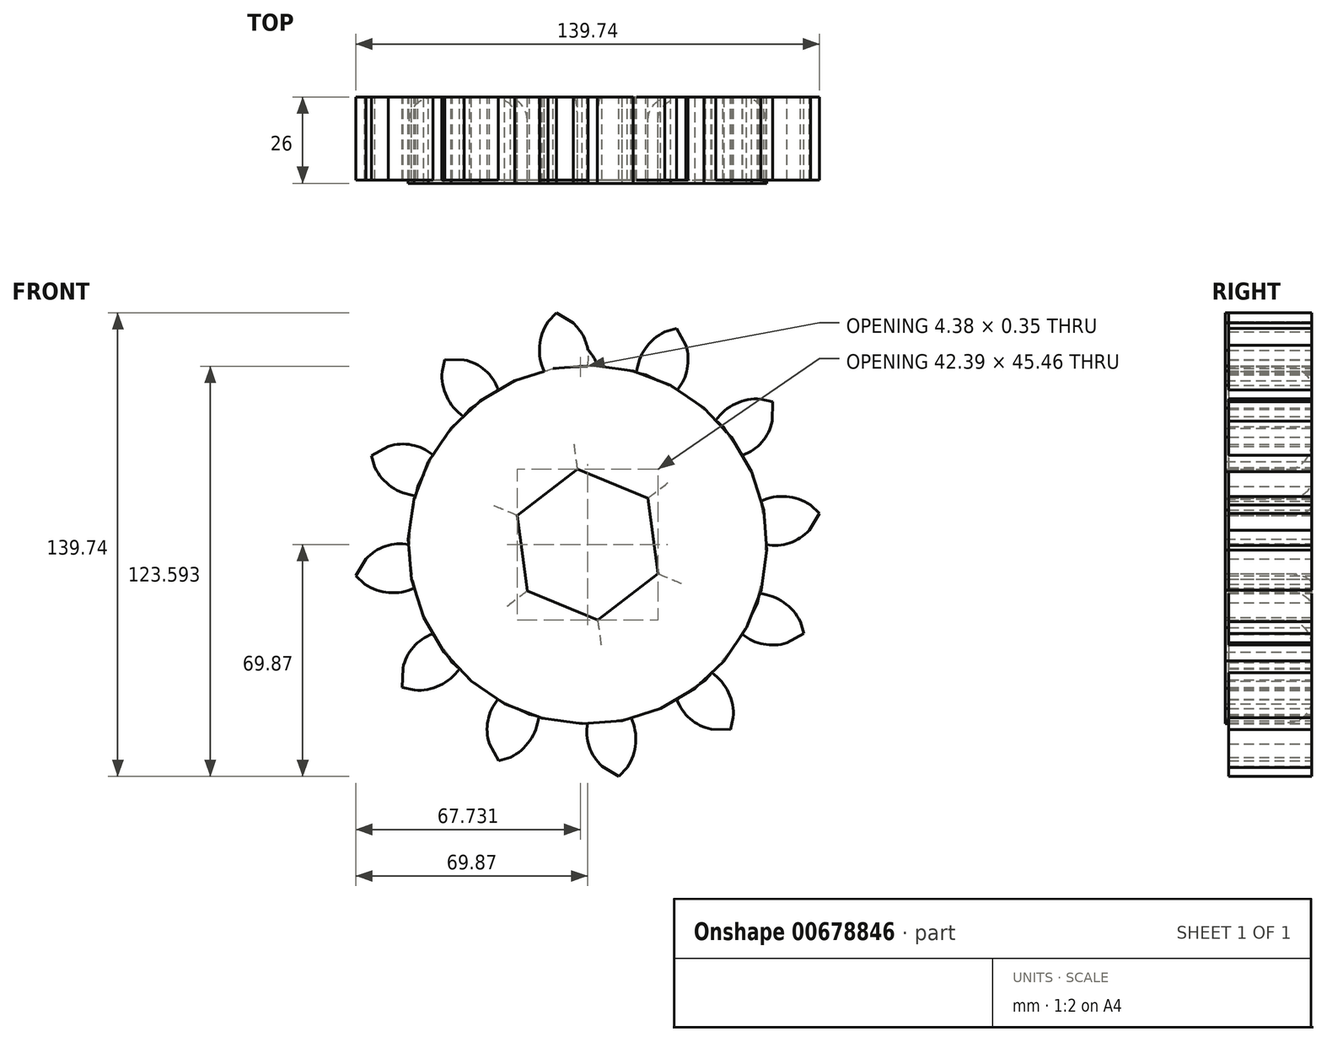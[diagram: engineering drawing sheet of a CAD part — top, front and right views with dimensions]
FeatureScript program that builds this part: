
annotation { "Feature Type Name" : "Feature", "Feature Type Description" : "" }
export const myFeature = defineFeature(function(context is Context, id is Id, definition is map)
    precondition{}
    {
        {
            var Q0;
            Q0=qCreatedBy(makeId("Front.planeOp"),FACE);
            var sketch = newSketch(context, id + "F0", { "sketchPlane" : qUnion([Q0])});
            skCircle(sketch, "E0", {"center": v(0, 0) * mm, "radius": 53.72 * mm, "construction": true});
            skCircle(sketch, "E1", {"center": v(0, 0) * mm, "radius": 58.67 * mm, "construction": true});
            skCircle(sketch, "E2", {"center": v(0, 0) * mm, "radius": 63.5 * mm, "construction": true});
            skLineSegment(sketch, "E3", {"start": v(0, 0) * mm, "end": v(0, 75.67) * mm, "construction": true});
            skLineSegment(sketch, "E4", {"start": v(0, 0) * mm, "end": v(-5.82, 88.8) * mm, "construction": true});
            skLineSegment(sketch, "E5", {"start": v(0, 58.67) * mm, "end": v(-75.23, 45.45) * mm, "construction": true});
            skLineSegment(sketch, "E6", {"start": v(0, 58.67) * mm, "end": v(-71.15, 58.67) * mm, "construction": true});
            skCircle(sketch, "E7", {"center": v(0, 0) * mm, "radius": 57.79 * mm, "construction": true});
            skCircle(sketch, "E8", {"center": v(0, 58.67) * mm, "radius": 14.6 * mm, "construction": true});
            skCircle(sketch, "E9", {"center": v(-14.38, 56.14) * mm, "radius": 14.6 * mm, "construction": true});
            skArc(sketch, "E10", {"start": v(0, 44.07) * mm, "mid": v(3.24, 51.37) * mm, "end": v(0, 58.67) * mm});
            skLineSegment(sketch, "E11.MirrorCS", {"start": v(0, 0) * mm, "end": v(5.82, 88.8) * mm, "construction": true});
            skArc(sketch, "E12", {"start": v(0.02, 53.72) * mm, "mid": v(-0.47, 60.83) * mm, "end": v(-4.38, 66.78) * mm});
            skArc(sketch, "E13", {"start": v(-11.9, 67.15) * mm, "mid": v(-14.49, 59.78) * mm, "end": v(-13.05, 52.11) * mm});
            skLineSegment(sketch, "E14", {"start": v(-11.9, 67.15) * mm, "end": v(-9.38, 69.87) * mm});
            skLineSegment(sketch, "E15", {"start": v(-9.38, 69.87) * mm, "end": v(-4.38, 66.78) * mm});
            skLineSegment(sketch, "E16.0", {"start": v(35.02, 41.18) * mm, "end": v(43.3, 32.36) * mm});
            skLineSegment(sketch, "E16.1", {"start": v(43.3, 32.36) * mm, "end": v(49.42, 21.91) * mm});
            skLineSegment(sketch, "E16.2", {"start": v(49.42, 21.91) * mm, "end": v(53.06, 10.36) * mm});
            skLineSegment(sketch, "E16.3", {"start": v(53.06, 10.36) * mm, "end": v(54.03, -1.7) * mm});
            skLineSegment(sketch, "E16.4", {"start": v(54.03, -1.7) * mm, "end": v(52.3, -13.68) * mm});
            skLineSegment(sketch, "E16.5", {"start": v(52.3, -13.68) * mm, "end": v(47.94, -24.98) * mm});
            skLineSegment(sketch, "E16.6", {"start": v(47.94, -24.98) * mm, "end": v(41.18, -35.02) * mm});
            skLineSegment(sketch, "E16.7", {"start": v(41.18, -35.02) * mm, "end": v(32.36, -43.3) * mm});
            skLineSegment(sketch, "E16.8", {"start": v(32.36, -43.3) * mm, "end": v(21.91, -49.42) * mm});
            skLineSegment(sketch, "E16.9", {"start": v(21.91, -49.42) * mm, "end": v(10.36, -53.06) * mm});
            skLineSegment(sketch, "E16.10", {"start": v(10.36, -53.06) * mm, "end": v(-1.7, -54.03) * mm});
            skLineSegment(sketch, "E16.11", {"start": v(-1.7, -54.03) * mm, "end": v(-13.68, -52.3) * mm});
            skLineSegment(sketch, "E16.12", {"start": v(-13.68, -52.3) * mm, "end": v(-24.98, -47.94) * mm});
            skLineSegment(sketch, "E16.13", {"start": v(-24.98, -47.94) * mm, "end": v(-35.02, -41.18) * mm});
            skLineSegment(sketch, "E16.14", {"start": v(-35.02, -41.18) * mm, "end": v(-43.3, -32.36) * mm});
            skLineSegment(sketch, "E16.15", {"start": v(-43.3, -32.36) * mm, "end": v(-49.42, -21.91) * mm});
            skLineSegment(sketch, "E16.16", {"start": v(-49.42, -21.91) * mm, "end": v(-53.06, -10.36) * mm});
            skLineSegment(sketch, "E16.17", {"start": v(-53.06, -10.36) * mm, "end": v(-54.03, 1.7) * mm});
            skLineSegment(sketch, "E16.18", {"start": v(-54.03, 1.7) * mm, "end": v(-52.3, 13.68) * mm});
            skLineSegment(sketch, "E16.19", {"start": v(-52.3, 13.68) * mm, "end": v(-47.94, 24.98) * mm});
            skLineSegment(sketch, "E16.20", {"start": v(-47.94, 24.98) * mm, "end": v(-41.18, 35.02) * mm});
            skLineSegment(sketch, "E16.21", {"start": v(-41.18, 35.02) * mm, "end": v(-32.36, 43.3) * mm});
            skLineSegment(sketch, "E16.22", {"start": v(-32.36, 43.3) * mm, "end": v(-21.91, 49.42) * mm});
            skLineSegment(sketch, "E16.23", {"start": v(-21.91, 49.42) * mm, "end": v(-10.36, 53.06) * mm});
            skLineSegment(sketch, "E16.24", {"start": v(-10.36, 53.06) * mm, "end": v(1.7, 54.03) * mm});
            skLineSegment(sketch, "E16.25", {"start": v(1.7, 54.03) * mm, "end": v(13.68, 52.3) * mm});
            skLineSegment(sketch, "E16.26", {"start": v(13.68, 52.3) * mm, "end": v(24.98, 47.94) * mm});
            skLineSegment(sketch, "E16.27", {"start": v(24.98, 47.94) * mm, "end": v(35.02, 41.18) * mm});
            skPoint(sketch, "E16.0.midPoint", {"position": v(39.16, 36.77) * mm});
            skCircle(sketch, "E17", {"center": v(0, 0) * mm, "radius": 53.72 * mm});
            skCircle(sketch, "E18", {"center": v(0, 0) * mm, "radius": 38.98 * mm});
            skCircle(sketch, "E19.cCircle", {"center": v(0, 0) * mm, "radius": 19.86 * mm, "construction": true});
            skLineSegment(sketch, "E19.0", {"start": v(-3.02, 22.73) * mm, "end": v(18.17, 13.98) * mm});
            skLineSegment(sketch, "E19.1", {"start": v(18.17, 13.98) * mm, "end": v(21.2, -8.75) * mm});
            skLineSegment(sketch, "E19.2", {"start": v(21.2, -8.75) * mm, "end": v(3.02, -22.73) * mm});
            skLineSegment(sketch, "E19.3", {"start": v(3.02, -22.73) * mm, "end": v(-18.17, -13.98) * mm});
            skLineSegment(sketch, "E19.4", {"start": v(-18.17, -13.98) * mm, "end": v(-21.2, 8.75) * mm});
            skLineSegment(sketch, "E19.5", {"start": v(-21.2, 8.75) * mm, "end": v(-3.02, 22.73) * mm});
            skPoint(sketch, "E19.0.midPoint", {"position": v(7.58, 18.36) * mm});
            skSolve(sketch);
        }
        {
            var Q0;
            {var subQ0=sQuery(id+"F0.wireOp",EDGE,"E14");Q0=makeQuery(id+"F0.imprint","IMPRINT",FACE,{"disambiguationData":[TD([[makeQuery(id+"F0.imprint","IMPRINT",EDGE,{"derivedFrom":subQ0}),-1.0]])]});}
            var Q1;
            {var subQ0=sQuery(id+"F0.wireOp",EDGE,"E17");var subQ17=makeQuery(id+"F0.imprint","INTERSECT",VERTEX,{"derivedFrom":[sQuery(id+"F0.wireOp",EDGE,"E16.2"),subQ0]});Q1=makeQuery(id+"F0.imprint","IMPRINT",FACE,{"disambiguationData":[TD([[makeQuery(id+"F0.imprint","IMPRINT",EDGE,{"disambiguationData":[TD([[subQ17,1.0]])],"derivedFrom":subQ0}),1.0]])]});}
            var Q2;
            Q2=makeQuery(id+"F0.imprint","IMPRINT",FACE,{"disambiguationData":[TD([[makeQuery(id+"F0.imprint","IMPRINT",EDGE,{"derivedFrom":sQuery(id+"F0.wireOp",EDGE,"E18")}),1.0]])]});
            extrude(context, id + "F1", {"entities" : qUnion([Q0, Q1, Q2]), "depth" : 25 * mm, "offsetDistance" : 25 * mm});
        }
        {
            var Q0;
            Q0=makeQuery(id+"F1.opExtrude","SWEPT_BODY",BODY,{"disambiguationData":[OSD([sQuery(id+"F0.wireOp",EDGE,"E12"),sQuery(id+"F0.wireOp",EDGE,"E13"),sQuery(id+"F0.wireOp",EDGE,"E14"),sQuery(id+"F0.wireOp",EDGE,"E15"),sQuery(id+"F0.wireOp",EDGE,"E16.23"),sQuery(id+"F0.wireOp",EDGE,"E16.24")])]});
            var Q1;
            Q1=makeQuery(id+"F1.opExtrude","SWEPT_FACE",FACE,{"disambiguationData":[OSD([sQuery(id+"F0.wireOp",EDGE,"E17")])]});
            circularPattern(context, id + "F2", {"operationType" : NewBodyOperationType.ADD, "entities" : qUnion([Q0]), "axis" : qUnion([Q1]), "angle" : 360 * degree, "instanceCount" : 12, "equalSpace" : true});
        }
        {
            var Q0;
            Q0 = qSketchRegion(id + "F0", true);
            var Q1;
            Q1=makeQuery(id+"F0.imprint","IMPRINT",FACE,{"disambiguationData":[TD([[makeQuery(id+"F0.imprint","IMPRINT",EDGE,{"derivedFrom":sQuery(id+"F0.wireOp",EDGE,"E18")}),1.0]])]});
            extrude(context, id + "F3", {"entities" : qUnion([Q0, Q1]), "depth" : 26 * mm, "offsetDistance" : 25 * mm});
        }
        {
            var Q0;
            Q0=makeQuery(id+"F1.opExtrude","CAP_FACE",FACE,{"disambiguationData":[OSD([sQuery(id+"F0.wireOp",EDGE,"E17"),sQuery(id+"F0.wireOp",EDGE,"E19.0"),sQuery(id+"F0.wireOp",EDGE,"E19.1"),sQuery(id+"F0.wireOp",EDGE,"E19.2"),sQuery(id+"F0.wireOp",EDGE,"E19.3"),sQuery(id+"F0.wireOp",EDGE,"E19.4"),sQuery(id+"F0.wireOp",EDGE,"E19.5")])],"isStart":true});
            fillet(context, id + "F4", {"entities" : qUnion([Q0]), "radius" : 7.24 * mm, "tangentPropagation" : true, "allowEdgeOverflow" : false});
        }
    });
